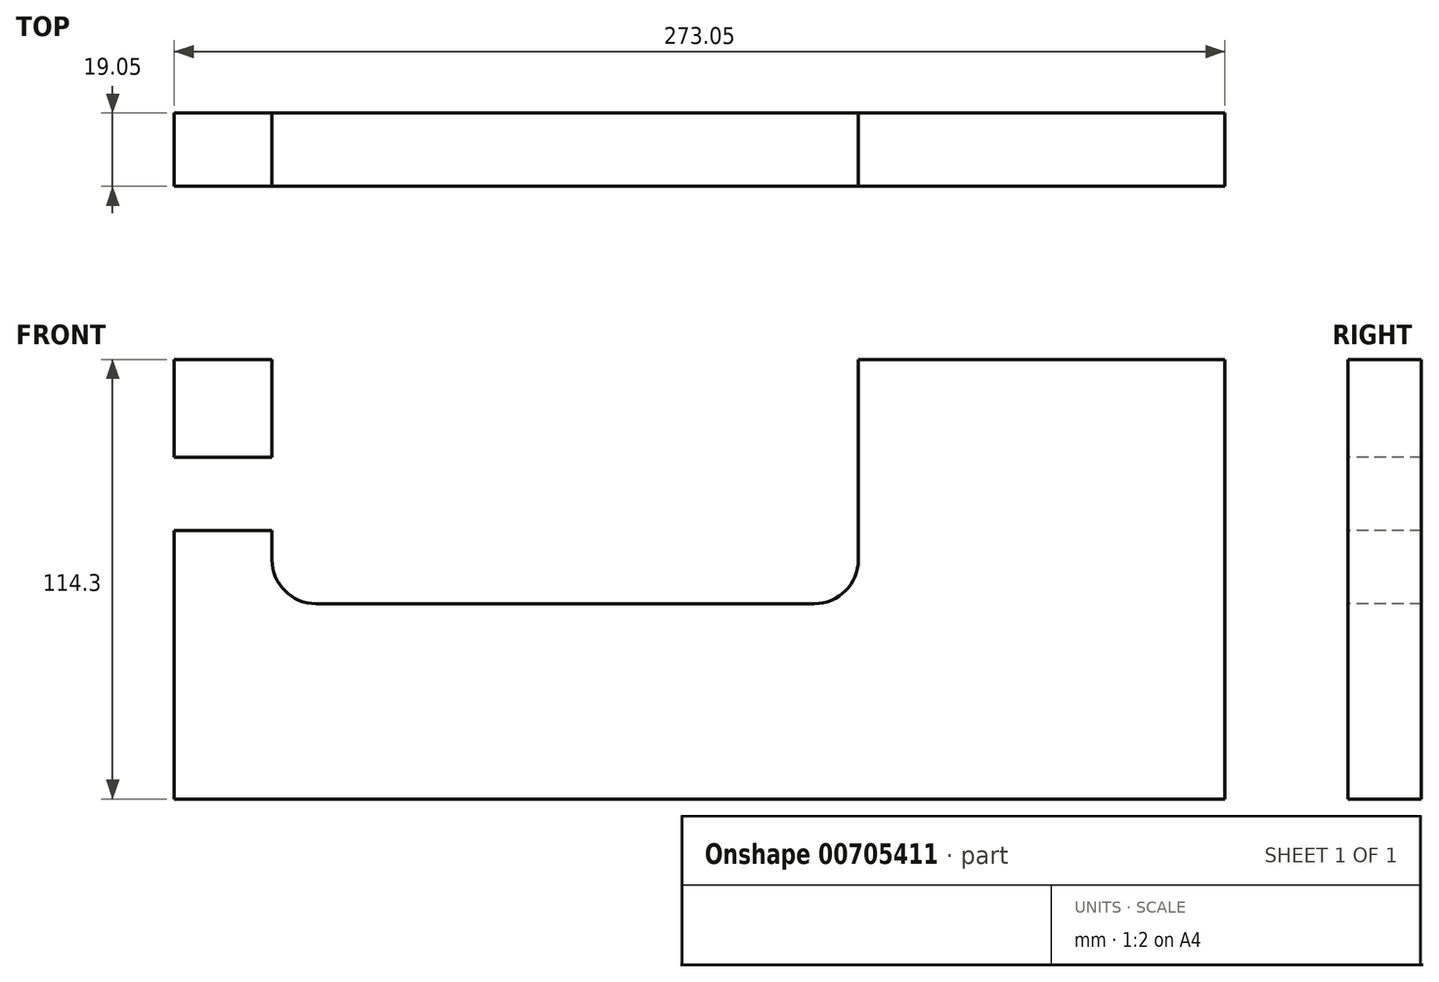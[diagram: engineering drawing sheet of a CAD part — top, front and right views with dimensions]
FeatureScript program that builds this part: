
annotation { "Feature Type Name" : "Feature", "Feature Type Description" : "" }
export const myFeature = defineFeature(function(context is Context, id is Id, definition is map)
    precondition{}
    {
        {
            var Q0;
            Q0=qCreatedBy(makeId("Front.planeOp"),FACE);
            var sketch = newSketch(context, id + "F0", { "sketchPlane" : qUnion([Q0])});
            skLineSegment(sketch, "E0.bottom", {"start": v(0, 0) * mm, "end": v(273.05, 0) * mm});
            skLineSegment(sketch, "E0.top", {"start": v(0, 114.3) * mm, "end": v(273.05, 114.3) * mm});
            skLineSegment(sketch, "E0.left", {"start": v(0, 0) * mm, "end": v(0, 114.3) * mm});
            skLineSegment(sketch, "E0.right", {"start": v(273.05, 0) * mm, "end": v(273.05, 114.3) * mm});
            skSolve(sketch);
        }
        {
            var Q0;
            Q0=qSketchRegion(id+"F0",true);
            extrude(context, id + "F1", {"entities" : qUnion([Q0]), "depth" : 19.05 * mm, "offsetDistance" : 25.4 * mm});
        }
        {
            var Q0;
            Q0=makeQuery(id+"F1.opExtrude","CAP_FACE",FACE,{"disambiguationData":[OSD([sQuery(id+"F0.wireOp",EDGE,"E0.bottom"),sQuery(id+"F0.wireOp",EDGE,"E0.top"),sQuery(id+"F0.wireOp",EDGE,"E0.left"),sQuery(id+"F0.wireOp",EDGE,"E0.right")])],"isStart":false});
            var sketch = newSketch(context, id + "F2", { "sketchPlane" : qUnion([Q0])});
            skLineSegment(sketch, "E1.bottom", {"start": v(0, 88.9) * mm, "end": v(25.4, 88.9) * mm});
            skLineSegment(sketch, "E1.top", {"start": v(0, 69.85) * mm, "end": v(25.4, 69.85) * mm});
            skLineSegment(sketch, "E1.left", {"start": v(0, 88.9) * mm, "end": v(0, 69.85) * mm});
            skLineSegment(sketch, "E1.right", {"start": v(25.4, 88.9) * mm, "end": v(25.4, 69.85) * mm});
            skLineSegment(sketch, "E2.bottom", {"start": v(25.4, 114.3) * mm, "end": v(177.8, 114.3) * mm});
            skLineSegment(sketch, "E2.top", {"start": v(36.83, 50.8) * mm, "end": v(166.37, 50.8) * mm});
            skLineSegment(sketch, "E2.left", {"start": v(25.4, 114.3) * mm, "end": v(25.4, 62.23) * mm});
            skLineSegment(sketch, "E2.right", {"start": v(177.8, 114.3) * mm, "end": v(177.8, 62.23) * mm});
            skPoint(sketch, "E3.visualSharp", {"position": v(25.4, 50.8) * mm});
            skArc(sketch, "E3.filletArc", {"start": v(25.4, 62.23) * mm, "mid": v(28.75, 54.15) * mm, "end": v(36.83, 50.8) * mm});
            skPoint(sketch, "E4.visualSharp", {"position": v(177.8, 50.8) * mm});
            skArc(sketch, "E4.filletArc", {"start": v(166.37, 50.8) * mm, "mid": v(174.45, 54.15) * mm, "end": v(177.8, 62.23) * mm});
            skSolve(sketch);
        }
        {
            var Q0;
            Q0=qSketchRegion(id+"F2",true);
            extrude(context, id + "F3", {"entities" : qUnion([Q0]), "operationType" : NewBodyOperationType.REMOVE, "oppositeDirection" : true, "depth" : 25.4 * mm, "offsetDistance" : 25.4 * mm});
        }
    });
